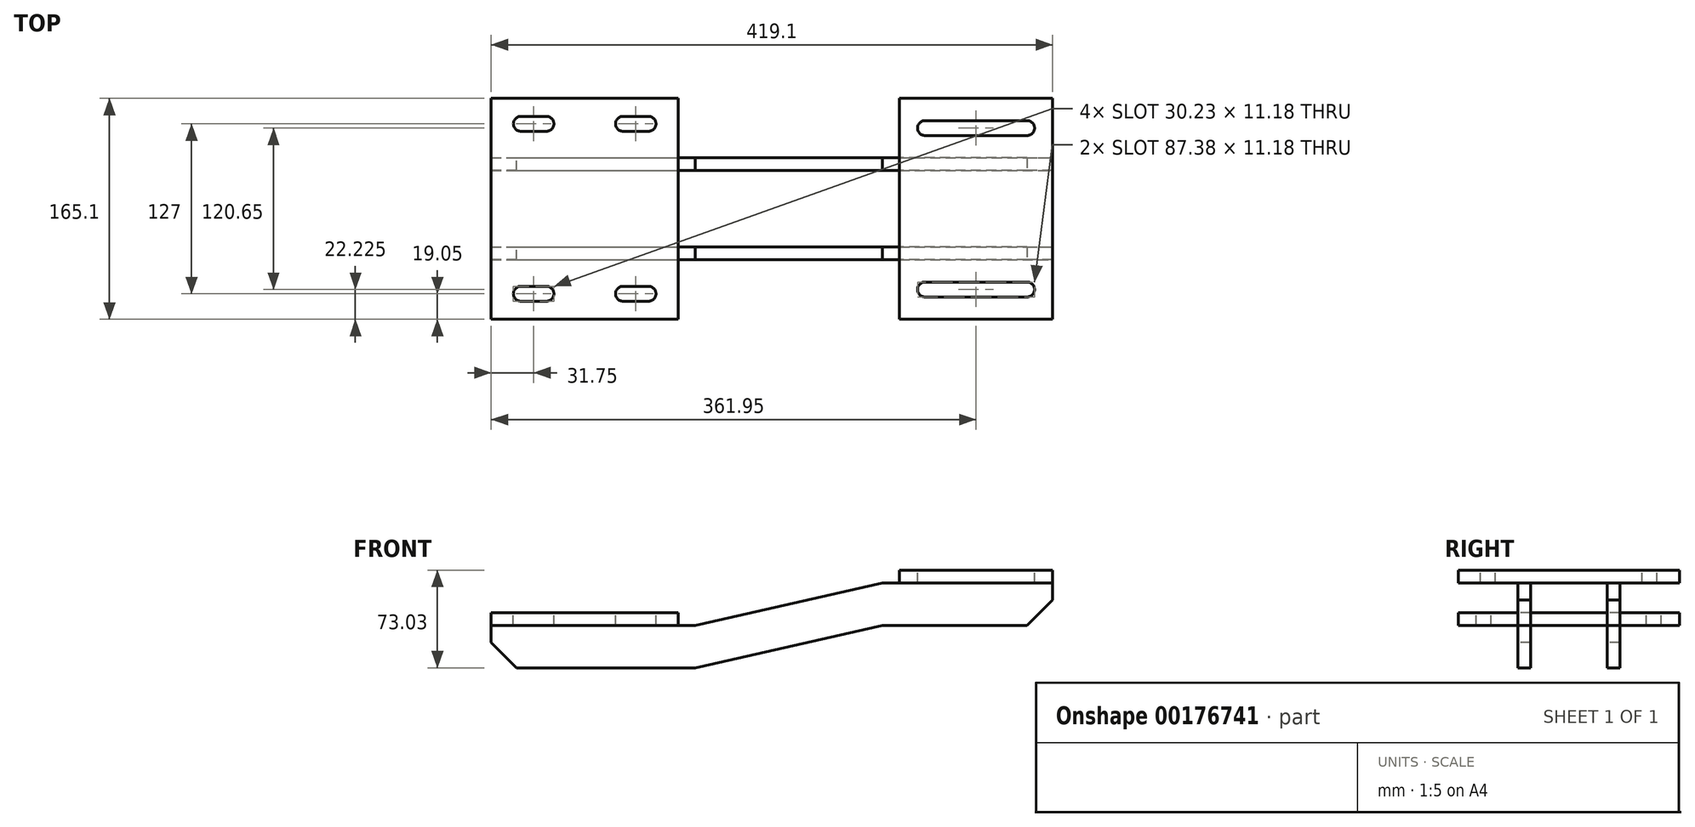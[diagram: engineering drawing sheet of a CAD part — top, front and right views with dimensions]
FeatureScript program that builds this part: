
annotation { "Feature Type Name" : "Feature", "Feature Type Description" : "" }
export const myFeature = defineFeature(function(context is Context, id is Id, definition is map)
    precondition{}
    {
        {
            var Q0;
            Q0=qCreatedBy(makeId("Top.planeOp"),FACE);
            var sketch = newSketch(context, id + "F0", { "sketchPlane" : qUnion([Q0])});
            skLineSegment(sketch, "E0.bottom", {"start": v(-69.85, 82.55) * mm, "end": v(69.85, 82.55) * mm});
            skLineSegment(sketch, "E0.top", {"start": v(-69.85, -82.55) * mm, "end": v(69.85, -82.55) * mm});
            skLineSegment(sketch, "E0.left", {"start": v(-69.85, 82.55) * mm, "end": v(-69.85, -82.55) * mm});
            skLineSegment(sketch, "E0.right", {"start": v(69.85, 82.55) * mm, "end": v(69.85, -82.55) * mm});
            skPoint(sketch, "E0.middle", {"position": v(0, 0) * mm});
            skLineSegment(sketch, "E1", {"start": v(-69.85, 0) * mm, "end": v(69.85, 0) * mm, "construction": true});
            skLineSegment(sketch, "E2", {"start": v(0, 82.55) * mm, "end": v(0, -82.55) * mm, "construction": true});
            skLineSegment(sketch, "E3.0", {"start": v(-47.62, 63.5) * mm, "end": v(-28.57, 63.5) * mm, "construction": true});
            skLineSegment(sketch, "E4.0", {"start": v(-38.1, 82.55) * mm, "end": v(-38.1, -82.55) * mm, "construction": true});
            skLineSegment(sketch, "E5.0", {"start": v(-47.62, 82.55) * mm, "end": v(-47.63, -82.55) * mm, "construction": true});
            skLineSegment(sketch, "E6.0", {"start": v(-28.57, 82.55) * mm, "end": v(-28.58, -82.55) * mm, "construction": true});
            skLineSegment(sketch, "E7.trimOffspring", {"start": v(0, 63.5) * mm, "end": v(69.85, 63.5) * mm, "construction": true});
            skArc(sketch, "E8.0.startCap", {"start": v(-47.62, 57.91) * mm, "mid": v(-53.21, 63.5) * mm, "end": v(-47.62, 69.09) * mm});
            skArc(sketch, "E8.0.endCap", {"start": v(-28.57, 69.09) * mm, "mid": v(-22.99, 63.5) * mm, "end": v(-28.57, 57.91) * mm});
            skLineSegment(sketch, "E8.0.left", {"start": v(-47.62, 69.09) * mm, "end": v(-28.57, 69.09) * mm});
            skLineSegment(sketch, "E8.0.right", {"start": v(-47.62, 57.91) * mm, "end": v(-28.57, 57.91) * mm});
            skArc(sketch, "E9.MirrorCS", {"start": v(-28.57, 57.91) * mm, "mid": v(-22.99, 63.5) * mm, "end": v(-28.57, 69.09) * mm});
            skArc(sketch, "E10.MirrorCS", {"start": v(-47.62, 69.09) * mm, "mid": v(-53.21, 63.5) * mm, "end": v(-47.62, 57.91) * mm});
            skArc(sketch, "E11.MirrorCS", {"start": v(47.63, 57.91) * mm, "mid": v(53.21, 63.5) * mm, "end": v(47.63, 69.09) * mm});
            skLineSegment(sketch, "E12.MirrorCS", {"start": v(47.63, 57.91) * mm, "end": v(28.58, 57.91) * mm});
            skArc(sketch, "E13.MirrorCS", {"start": v(28.58, 57.91) * mm, "mid": v(22.99, 63.5) * mm, "end": v(28.58, 69.09) * mm});
            skLineSegment(sketch, "E14.MirrorCS", {"start": v(47.63, 69.09) * mm, "end": v(28.58, 69.09) * mm});
            skArc(sketch, "E15.MirrorCS", {"start": v(47.63, 69.09) * mm, "mid": v(53.21, 63.5) * mm, "end": v(47.63, 57.91) * mm});
            skArc(sketch, "E16.MirrorCS", {"start": v(28.58, 69.09) * mm, "mid": v(22.99, 63.5) * mm, "end": v(28.58, 57.91) * mm});
            skLineSegment(sketch, "E17.MirrorCS", {"start": v(47.63, 63.5) * mm, "end": v(28.58, 63.5) * mm, "construction": true});
            skLineSegment(sketch, "E18.MirrorCS", {"start": v(47.63, -57.91) * mm, "end": v(28.58, -57.91) * mm});
            skArc(sketch, "E19.MirrorCS", {"start": v(-47.62, -57.91) * mm, "mid": v(-53.21, -63.5) * mm, "end": v(-47.62, -69.09) * mm});
            skLineSegment(sketch, "E20.MirrorCS", {"start": v(47.63, -69.09) * mm, "end": v(28.58, -69.09) * mm});
            skLineSegment(sketch, "E21.MirrorCS", {"start": v(-47.62, -57.91) * mm, "end": v(-28.57, -57.91) * mm});
            skArc(sketch, "E22.MirrorCS", {"start": v(47.63, -69.09) * mm, "mid": v(53.21, -63.5) * mm, "end": v(47.63, -57.91) * mm});
            skArc(sketch, "E23.MirrorCS", {"start": v(28.58, -57.91) * mm, "mid": v(22.99, -63.5) * mm, "end": v(28.58, -69.09) * mm});
            skLineSegment(sketch, "E24.MirrorCS", {"start": v(-47.62, -69.09) * mm, "end": v(-28.57, -69.09) * mm});
            skArc(sketch, "E25.MirrorCS", {"start": v(-28.57, -57.91) * mm, "mid": v(-22.99, -63.5) * mm, "end": v(-28.57, -69.09) * mm});
            skArc(sketch, "E26.MirrorCS", {"start": v(-47.62, -69.09) * mm, "mid": v(-53.21, -63.5) * mm, "end": v(-47.62, -57.91) * mm});
            skArc(sketch, "E27.MirrorCS", {"start": v(28.58, -69.09) * mm, "mid": v(22.99, -63.5) * mm, "end": v(28.58, -57.91) * mm});
            skLineSegment(sketch, "E28.MirrorCS", {"start": v(47.63, -63.5) * mm, "end": v(28.58, -63.5) * mm, "construction": true});
            skArc(sketch, "E29.MirrorCS", {"start": v(-28.57, -69.09) * mm, "mid": v(-22.99, -63.5) * mm, "end": v(-28.57, -57.91) * mm});
            skLineSegment(sketch, "E30.MirrorCS", {"start": v(-47.62, -63.5) * mm, "end": v(-28.57, -63.5) * mm, "construction": true});
            skArc(sketch, "E31.MirrorCS", {"start": v(47.63, -57.91) * mm, "mid": v(53.21, -63.5) * mm, "end": v(47.63, -69.09) * mm});
            skSolve(sketch);
        }
        {
            var Q0;
            Q0 = qSketchRegion(id + "F0", true);
            extrude(context, id + "F1", {"entities" : qUnion([Q0]), "oppositeDirection" : true, "depth" : 9.52 * mm});
        }
        {
            var Q0;
            Q0=makeQuery(id+"F1.opExtrude","CAP_FACE",FACE,{"disambiguationData":[OSD([sQuery(id+"F0.wireOp",EDGE,"E0.bottom"),sQuery(id+"F0.wireOp",EDGE,"E0.top"),sQuery(id+"F0.wireOp",EDGE,"E0.left"),sQuery(id+"F0.wireOp",EDGE,"E0.right"),sQuery(id+"F0.wireOp",EDGE,"E8.0.left"),sQuery(id+"F0.wireOp",EDGE,"E8.0.right"),sQuery(id+"F0.wireOp",EDGE,"E9.MirrorCS"),sQuery(id+"F0.wireOp",EDGE,"E10.MirrorCS"),sQuery(id+"F0.wireOp",EDGE,"E12.MirrorCS"),sQuery(id+"F0.wireOp",EDGE,"E15.MirrorCS"),sQuery(id+"F0.wireOp",EDGE,"E16.MirrorCS"),sQuery(id+"F0.wireOp",EDGE,"E14.MirrorCS"),sQuery(id+"F0.wireOp",EDGE,"E21.MirrorCS"),sQuery(id+"F0.wireOp",EDGE,"E26.MirrorCS"),sQuery(id+"F0.wireOp",EDGE,"E18.MirrorCS"),sQuery(id+"F0.wireOp",EDGE,"E20.MirrorCS"),sQuery(id+"F0.wireOp",EDGE,"E27.MirrorCS"),sQuery(id+"F0.wireOp",EDGE,"E29.MirrorCS"),sQuery(id+"F0.wireOp",EDGE,"E24.MirrorCS"),sQuery(id+"F0.wireOp",EDGE,"E31.MirrorCS")])],"isStart":true});
            cPlane(context, id + "F2", {"entities" : qUnion([Q0]), "cplaneType" : CPlaneType.OFFSET, "offset" : 31.75 * mm, "width" : 152.4 * mm, "height" : 152.4 * mm});
        }
        {
            var Q0;
            Q0=qCreatedBy(id+"F2.planeOp",FACE);
            var sketch = newSketch(context, id + "F3", { "sketchPlane" : qUnion([Q0])});
            skLineSegment(sketch, "E32.0.0", {"start": v(69.85, 82.55) * mm, "end": v(-69.85, 82.55) * mm, "construction": true});
            skLineSegment(sketch, "E32.0.1", {"start": v(-69.85, 82.55) * mm, "end": v(-69.85, -82.55) * mm, "construction": true});
            skLineSegment(sketch, "E32.0.2", {"start": v(-69.85, -82.55) * mm, "end": v(69.85, -82.55) * mm, "construction": true});
            skLineSegment(sketch, "E32.0.3", {"start": v(69.85, -82.55) * mm, "end": v(69.85, 82.55) * mm, "construction": true});
            skPoint(sketch, "E33.0", {"position": v(22.99, -63.5) * mm});
            skPoint(sketch, "E34.0", {"position": v(38.1, -57.91) * mm});
            skLineSegment(sketch, "E35", {"start": v(38.1, -57.91) * mm, "end": v(38.1, -117.62) * mm, "construction": true});
            skLineSegment(sketch, "E36.0", {"start": v(292.1, 0) * mm, "end": v(292.1, -117.62) * mm, "construction": true});
            skLineSegment(sketch, "E37", {"start": v(0, 0) * mm, "end": v(319.1, 0) * mm, "construction": true});
            skLineSegment(sketch, "E38.bottom", {"start": v(234.95, 82.55) * mm, "end": v(349.25, 82.55) * mm});
            skLineSegment(sketch, "E38.top", {"start": v(234.95, -82.55) * mm, "end": v(349.25, -82.55) * mm});
            skPoint(sketch, "E38.middle", {"position": v(292.1, 0) * mm});
            skLineSegment(sketch, "E39.0", {"start": v(254, 60.33) * mm, "end": v(330.2, 60.33) * mm, "construction": true});
            skLineSegment(sketch, "E40.0", {"start": v(330.2, 60.32) * mm, "end": v(330.2, -117.62) * mm, "construction": true});
            skLineSegment(sketch, "E41.0", {"start": v(254, 60.32) * mm, "end": v(254, -117.62) * mm, "construction": true});
            skLineSegment(sketch, "E42.0", {"start": v(349.25, 82.55) * mm, "end": v(349.25, -82.55) * mm});
            skLineSegment(sketch, "E43.0", {"start": v(234.95, 82.55) * mm, "end": v(234.95, -82.55) * mm});
            skPoint(sketch, "E44.orphan", {"position": v(241.3, 82.55) * mm});
            skPoint(sketch, "E45.orphan", {"position": v(342.9, 82.55) * mm});
            skPoint(sketch, "E46.orphan", {"position": v(342.9, -82.55) * mm});
            skPoint(sketch, "E47.orphan", {"position": v(241.3, -82.55) * mm});
            skArc(sketch, "E48.0.startCap", {"start": v(254, 54.74) * mm, "mid": v(248.41, 60.33) * mm, "end": v(254, 65.91) * mm});
            skArc(sketch, "E48.0.endCap", {"start": v(330.2, 65.91) * mm, "mid": v(335.79, 60.33) * mm, "end": v(330.2, 54.74) * mm});
            skLineSegment(sketch, "E48.0.left", {"start": v(254, 65.91) * mm, "end": v(330.2, 65.91) * mm});
            skLineSegment(sketch, "E48.0.right", {"start": v(254, 54.74) * mm, "end": v(330.2, 54.74) * mm});
            skArc(sketch, "E49.MirrorCS", {"start": v(254, -54.74) * mm, "mid": v(248.41, -60.33) * mm, "end": v(254, -65.91) * mm});
            skArc(sketch, "E50.MirrorCS", {"start": v(330.2, -65.91) * mm, "mid": v(335.79, -60.33) * mm, "end": v(330.2, -54.74) * mm});
            skLineSegment(sketch, "E51.MirrorCS", {"start": v(254, -65.91) * mm, "end": v(330.2, -65.91) * mm});
            skLineSegment(sketch, "E52.MirrorCS", {"start": v(254, -54.74) * mm, "end": v(330.2, -54.74) * mm});
            skLineSegment(sketch, "E53.MirrorCS", {"start": v(254, -60.33) * mm, "end": v(330.2, -60.33) * mm, "construction": true});
            skSolve(sketch);
        }
        {
            var Q0;
            Q0 = qSketchRegion(id + "F3", true);
            extrude(context, id + "F4", {"entities" : qUnion([Q0]), "oppositeDirection" : true, "depth" : 9.52 * mm});
        }
        {
            var Q0;
            Q0=qCreatedBy(makeId("Front.planeOp"),FACE);
            cPlane(context, id + "F5", {"entities" : qUnion([Q0]), "cplaneType" : CPlaneType.OFFSET, "offset" : 38.1 * mm, "width" : 152.4 * mm, "height" : 152.4 * mm});
        }
        {
            var Q0;
            Q0=qCreatedBy(id+"F5.planeOp",FACE);
            var sketch = newSketch(context, id + "F6", { "sketchPlane" : qUnion([Q0])});
            skLineSegment(sketch, "E54.0", {"start": v(-69.85, -9.53) * mm, "end": v(69.85, -9.53) * mm});
            skLineSegment(sketch, "E55.0", {"start": v(234.95, 22.23) * mm, "end": v(349.25, 22.23) * mm});
            skLineSegment(sketch, "E56.0", {"start": v(234.95, 22.23) * mm, "end": v(234.95, 31.75) * mm, "construction": true});
            skPoint(sketch, "E57.0", {"position": v(69.85, -4.76) * mm});
            skLineSegment(sketch, "E58", {"start": v(234.95, 22.23) * mm, "end": v(69.85, 22.23) * mm, "construction": true});
            skLineSegment(sketch, "E59", {"start": v(152.4, 22.23) * mm, "end": v(152.4, -20.32) * mm, "construction": true});
            skLineSegment(sketch, "E60.0", {"start": v(222.25, 22.23) * mm, "end": v(222.25, -20.32) * mm, "construction": true});
            skLineSegment(sketch, "E61.MirrorCS", {"start": v(82.55, 22.23) * mm, "end": v(82.55, -20.32) * mm, "construction": true});
            skLineSegment(sketch, "E62", {"start": v(69.85, -9.53) * mm, "end": v(82.55, -9.53) * mm});
            skLineSegment(sketch, "E63", {"start": v(82.55, -9.53) * mm, "end": v(222.25, 22.23) * mm});
            skLineSegment(sketch, "E64", {"start": v(222.25, 22.23) * mm, "end": v(234.95, 22.23) * mm});
            skLineSegment(sketch, "E65", {"start": v(-69.85, -9.53) * mm, "end": v(-69.85, -41.27) * mm});
            skLineSegment(sketch, "E66", {"start": v(-69.85, -41.27) * mm, "end": v(82.55, -41.27) * mm});
            skLineSegment(sketch, "E67", {"start": v(349.25, 22.23) * mm, "end": v(349.25, -9.52) * mm});
            skLineSegment(sketch, "E68", {"start": v(349.25, -9.52) * mm, "end": v(222.25, -9.53) * mm});
            skPoint(sketch, "E68.endSnap0", {"position": v(222.25, 0.95) * mm});
            skLineSegment(sketch, "E69", {"start": v(222.25, -9.53) * mm, "end": v(82.55, -41.27) * mm});
            skSolve(sketch);
        }
        {
            var Q0;
            Q0 = qSketchRegion(id + "F6", true);
            extrude(context, id + "F7", {"entities" : qUnion([Q0]), "oppositeDirection" : true, "depth" : 9.52 * mm});
        }
        {
            var Q0;
            Q0=makeQuery(id+"F7.opExtrude","SWEPT_BODY",BODY,{"disambiguationData":[OSD([sQuery(id+"F6.wireOp",EDGE,"E54.0"),sQuery(id+"F6.wireOp",EDGE,"E55.0"),sQuery(id+"F6.wireOp",EDGE,"E62"),sQuery(id+"F6.wireOp",EDGE,"E63"),sQuery(id+"F6.wireOp",EDGE,"E64"),sQuery(id+"F6.wireOp",EDGE,"E65"),sQuery(id+"F6.wireOp",EDGE,"E66"),sQuery(id+"F6.wireOp",EDGE,"E67"),sQuery(id+"F6.wireOp",EDGE,"E68"),sQuery(id+"F6.wireOp",EDGE,"E69")])]});
            var Q1;
            Q1=qCreatedBy(makeId("Front.planeOp"),FACE);
            mirror(context, id + "F8", {"entities" : qUnion([Q0]), "mirrorPlane" : qUnion([Q1])});
        }
        {
            var Q0;
            Q0=makeQuery(id+"F7.opExtrude","SWEPT_EDGE",EDGE,{"disambiguationData":[OSD([sQuery(id+"F6.wireOp",EDGE,"E65"),sQuery(id+"F6.wireOp",EDGE,"E66")])]});
            var Q1;
            Q1=makeQuery(id+"F8.opPattern","COPY",EDGE,{"derivedFrom":makeQuery(id+"F7.opExtrude","SWEPT_EDGE",EDGE,{"disambiguationData":[OSD([sQuery(id+"F6.wireOp",EDGE,"E65"),sQuery(id+"F6.wireOp",EDGE,"E66")])]}),"instanceName":"1"});
            var Q2;
            Q2=makeQuery(id+"F7.opExtrude","SWEPT_EDGE",EDGE,{"disambiguationData":[OSD([sQuery(id+"F6.wireOp",EDGE,"E67"),sQuery(id+"F6.wireOp",EDGE,"E68")])]});
            var Q3;
            Q3=makeQuery(id+"F8.opPattern","COPY",EDGE,{"derivedFrom":makeQuery(id+"F7.opExtrude","SWEPT_EDGE",EDGE,{"disambiguationData":[OSD([sQuery(id+"F6.wireOp",EDGE,"E67"),sQuery(id+"F6.wireOp",EDGE,"E68")])]}),"instanceName":"1"});
            chamfer(context, id + "F9", {"entities" : qUnion([Q0, Q1, Q2, Q3]), "width" : 19.05 * mm, "tangentPropagation" : true});
        }
    });
